FCSTD DOCUMENT  (FreeCAD 0.20R29177 (Git))
Label: bun bolt connector III
License: All rights reserved
LicenseURL: http://en.wikipedia.org/wiki/All_rights_reserved
objects: Sketcher::SketchObject×2, PartDesign::Pad×1, Part::Helix×1, PartDesign::ShapeBinder×1, PartDesign::Body×1
note: 7 computed .brp shape members not serialized (recipe doc carries the construction recipe); baked Part::Feature solids carry a one-line shape summary decoded from their .brp

FEATURE [Sketcher::SketchObject] Sketch
  FullyConstrained = true
  MapMode = 5
  Support = -> [XY_Plane]
  sketch-geometry (1):
    g0: Circle CenterX=0 CenterY=0 CenterZ=0 NormalX=0 NormalY=0 NormalZ=1 AngleXU=0 Radius=11.1
  constraints (2):
    c: Coincident(g0,g-1)
    c: Radius(g0) = 11.1
FEATURE [PartDesign::Pad] Pad
  Direction = (0,0,1)
  Length = 13
  Length2 = 10
  Profile = -> Sketch
  ReferenceAxis = -> Sketch [N_Axis]
  Type = 0
FEATURE [Sketcher::SketchObject] Sketch001  label="ThreadProfile"
  FullyConstrained = false
  MapMode = 5
  Placement = pos=(0,0,0) rot=(1,0,0;1.5708rad)
  Support = -> [XZ_Plane]
  sketch-geometry (4):
    g0: LineSegment StartX=10.75 StartY=8.22046 StartZ=0 EndX=10.75 EndY=11.7205 EndZ=0
    g1: LineSegment StartX=10.75 StartY=11.7205 StartZ=0 EndX=12 EndY=10.4705 EndZ=0
    g2: LineSegment StartX=12 StartY=10.4705 StartZ=0 EndX=12 EndY=9.47046 EndZ=0
    g3: LineSegment StartX=12 StartY=9.47046 StartZ=0 EndX=10.75 EndY=8.22046 EndZ=0
  constraints (11):
    c: Vertical(g0)
    c: Coincident(g0,g1)
    c: Coincident(g1,g2)
    c: Vertical(g2)
    c: Coincident(g2,g3)
    c: Coincident(g3,g0)
    c: Angle(g3,g0) = 0.785398
    c: Angle(g0,g1) = 0.785398
    c: DistanceY(g2,g2) = 1
    c: DistanceX(g3,g3) = 1.25
    c: DistanceX(g-1,g2) = 12
FEATURE [Part::Helix] Helix
  Angle = 0
  AttacherType = Attacher::AttachEngine3D
  Height = 12
  LocalCoord = 0
  Pitch = 2.5
  Placement = pos=(0,0,0.5) rot=(0,1,0;0.034907rad)
  Radius = 12
  SegmentLength = 0
  Style = 1
FEATURE [PartDesign::ShapeBinder] ShapeBinder
  Placement = pos=(0,0,0.5) rot=(0,1,0;0.034907rad)
  Support = -> [Helix]
  TraceSupport = false
FEATURE [PartDesign::Body] Body
  Group = -> [Sketch,Pad,Sketch001,ShapeBinder]
  Origin = -> Origin
